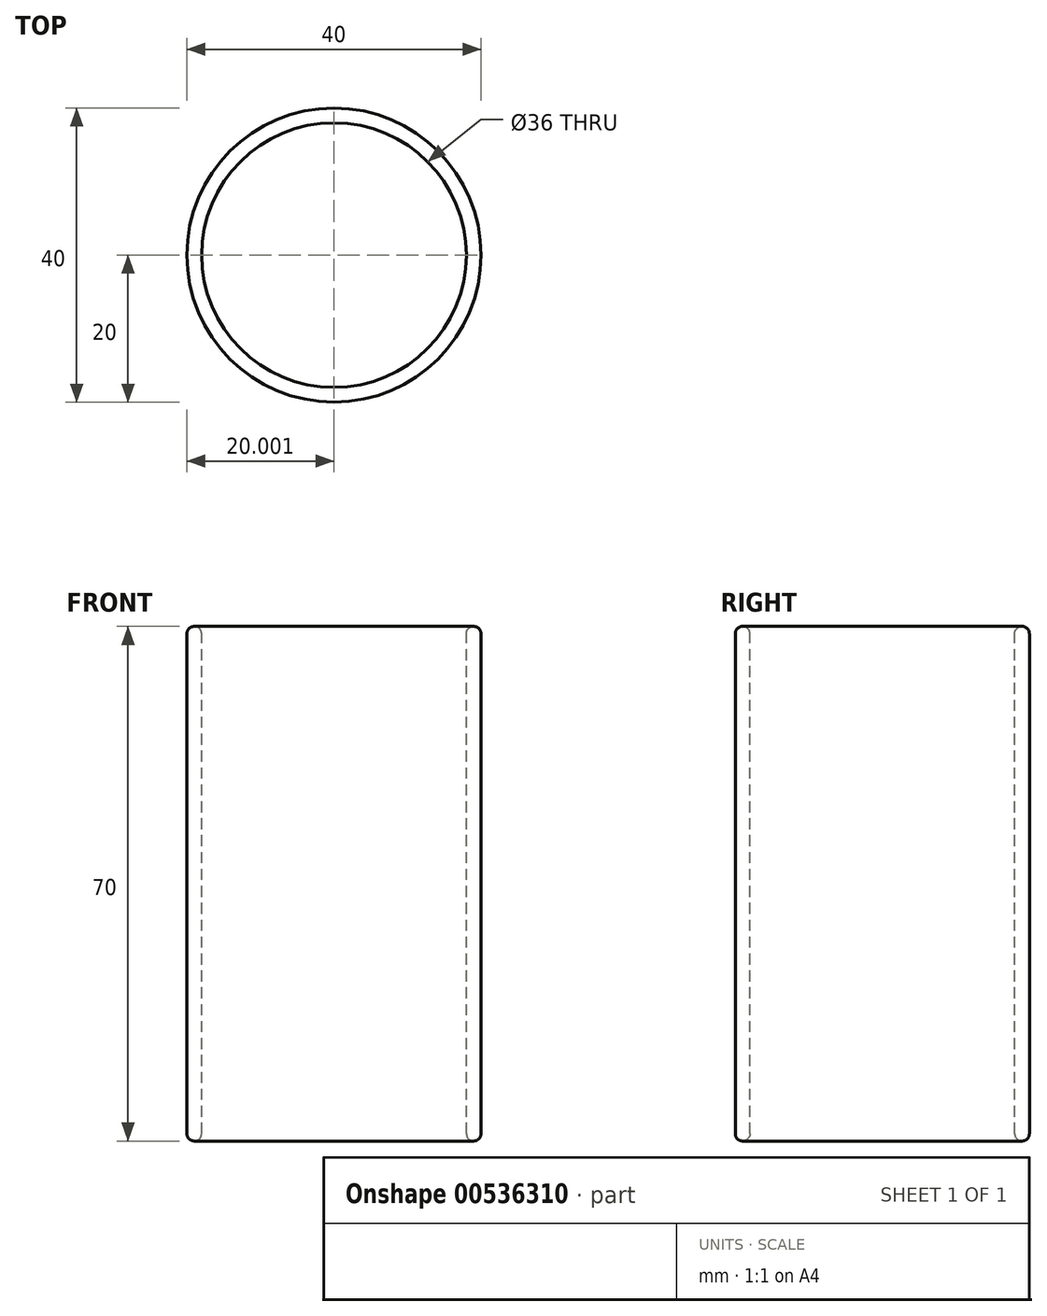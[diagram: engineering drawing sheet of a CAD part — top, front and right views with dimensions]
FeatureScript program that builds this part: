
annotation { "Feature Type Name" : "Feature", "Feature Type Description" : "" }
export const myFeature = defineFeature(function(context is Context, id is Id, definition is map)
    precondition{}
    {
        {
            var Q0;
            Q0=qCreatedBy(makeId("Front.planeOp"),FACE);
            var sketch = newSketch(context, id + "F0", { "sketchPlane" : qUnion([Q0])});
            skLineSegment(sketch, "E0.bottom", {"start": v(-8.9, 48.56) * mm, "end": v(-6.9, 48.56) * mm});
            skLineSegment(sketch, "E0.top", {"start": v(-8.9, -21.44) * mm, "end": v(-6.9, -21.44) * mm});
            skLineSegment(sketch, "E0.left", {"start": v(-8.9, 48.56) * mm, "end": v(-8.9, -21.44) * mm});
            skLineSegment(sketch, "E0.right", {"start": v(11.1, 48.56) * mm, "end": v(11.1, -21.44) * mm});
            skLineSegment(sketch, "E1.0", {"start": v(-6.9, 48.56) * mm, "end": v(-6.9, -21.44) * mm});
            skSolve(sketch);
        }
        {
            var Q0;
            Q0=qSketchRegion(id+"F0",true);
            var Q1;
            Q1=sQuery(id+"F0.wireOp",EDGE,"E0.right");
            revolve(context, id + "F1", {"entities" : qUnion([Q0]), "axis" : qUnion([Q1]), "revolveType" : RevolveType.FULL});
        }
        {
            var Q0;
            Q0=makeQuery(id+"F1.opRevolve","SWEPT_FACE",FACE,{"disambiguationData":[OSD([sQuery(id+"F0.wireOp",EDGE,"E0.bottom")])]});
            var Q1;
            Q1=makeQuery(id+"F1.opRevolve","SWEPT_FACE",FACE,{"disambiguationData":[OSD([sQuery(id+"F0.wireOp",EDGE,"E0.top")])]});
            fillet(context, id + "F2", {"entities" : qUnion([Q0, Q1]), "radius" : 1 * mm, "tangentPropagation" : true, "allowEdgeOverflow" : false});
        }
    });
